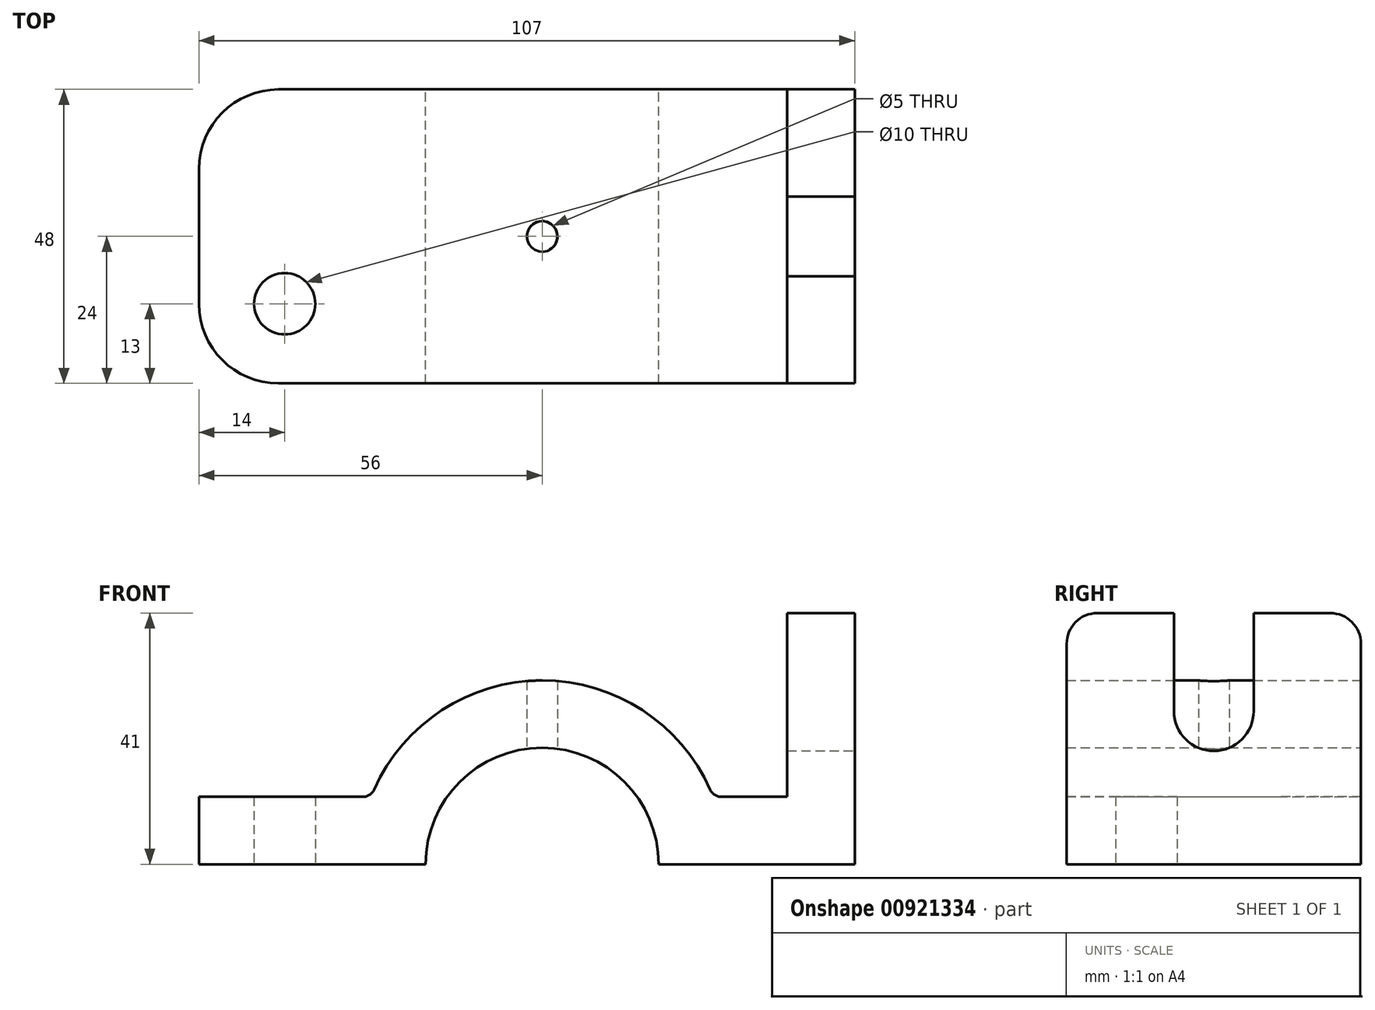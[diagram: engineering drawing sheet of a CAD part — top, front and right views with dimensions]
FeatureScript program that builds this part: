
annotation { "Feature Type Name" : "Feature", "Feature Type Description" : "" }
export const myFeature = defineFeature(function(context is Context, id is Id, definition is map)
    precondition{}
    {
        {
            var Q0;
            Q0=qCreatedBy(makeId("Front.planeOp"),FACE);
            var sketch = newSketch(context, id + "F0", { "sketchPlane" : qUnion([Q0])});
            skCircle(sketch, "E0", {"center": v(0, 0) * mm, "radius": 19 * mm});
            skCircle(sketch, "E1", {"center": v(0, 0) * mm, "radius": 30 * mm});
            skLineSegment(sketch, "E2.bottom", {"start": v(-56, 0) * mm, "end": v(51, 0) * mm});
            skLineSegment(sketch, "E2.top", {"start": v(-56, 11) * mm, "end": v(51, 11) * mm});
            skLineSegment(sketch, "E2.left", {"start": v(-56, 0) * mm, "end": v(-56, 11) * mm});
            skLineSegment(sketch, "E2.right", {"start": v(51, 0) * mm, "end": v(51, 11) * mm});
            skPoint(sketch, "E3", {"position": v(-2.5, 0) * mm});
            skLineSegment(sketch, "E4.bottom", {"start": v(51, 11) * mm, "end": v(40, 11) * mm});
            skLineSegment(sketch, "E4.top", {"start": v(51, 41) * mm, "end": v(40, 41) * mm});
            skLineSegment(sketch, "E4.left", {"start": v(51, 11) * mm, "end": v(51, 41) * mm});
            skLineSegment(sketch, "E4.right", {"start": v(40, 11) * mm, "end": v(40, 41) * mm});
            skSolve(sketch);
        }
        {
            var Q0;
            {var subQ5=sQuery(id+"F0.wireOp",EDGE,"E2.left");Q0=makeQuery(id+"F0.imprint","IMPRINT",FACE,{"disambiguationData":[TD([[makeQuery(id+"F0.imprint","IMPRINT",EDGE,{"derivedFrom":subQ5}),-1.0]])]});}
            var Q1;
            {var subQ0=sQuery(id+"F0.wireOp",EDGE,"E2.bottom");var subQ1=sQuery(id+"F0.wireOp",EDGE,"E0");var subQ2=makeQuery(id+"F0.imprint","INTERSECT",VERTEX,{"disambiguationData":[OD(0.0)],"derivedFrom":[subQ1,subQ0]});Q1=makeQuery(id+"F0.imprint","IMPRINT",FACE,{"disambiguationData":[TD([[makeQuery(id+"F0.imprint","IMPRINT",EDGE,{"disambiguationData":[TD([[subQ2,1.0]])],"derivedFrom":subQ1}),-1.0]])]});}
            var Q2;
            {var subQ0=sQuery(id+"F0.wireOp",EDGE,"E2.top");var subQ1=sQuery(id+"F0.wireOp",EDGE,"E0");var subQ2=makeQuery(id+"F0.imprint","INTERSECT",VERTEX,{"disambiguationData":[OD(0.0)],"derivedFrom":[subQ1,subQ0]});Q2=makeQuery(id+"F0.imprint","IMPRINT",FACE,{"disambiguationData":[TD([[makeQuery(id+"F0.imprint","IMPRINT",EDGE,{"disambiguationData":[TD([[subQ2,1.0]])],"derivedFrom":subQ1}),-1.0]])]});}
            var Q3;
            {var subQ0=sQuery(id+"F0.wireOp",EDGE,"E2.top");var subQ1=sQuery(id+"F0.wireOp",EDGE,"E0");var subQ2=makeQuery(id+"F0.imprint","INTERSECT",VERTEX,{"disambiguationData":[OD(1.0)],"derivedFrom":[subQ1,subQ0]});Q3=makeQuery(id+"F0.imprint","IMPRINT",FACE,{"disambiguationData":[TD([[makeQuery(id+"F0.imprint","IMPRINT",EDGE,{"disambiguationData":[TD([[subQ2,1.0]])],"derivedFrom":subQ1}),-1.0]])]});}
            var Q4;
            Q4=makeQuery(id+"F0.imprint","IMPRINT",FACE,{"disambiguationData":[TD([[makeQuery(id+"F0.imprint","IMPRINT",EDGE,{"derivedFrom":sQuery(id+"F0.wireOp",EDGE,"E4.top")}),1.0]])]});
            var Q5;
            {var subQ0=sQuery(id+"F0.wireOp",EDGE,"E2.right");Q5=makeQuery(id+"F0.imprint","IMPRINT",FACE,{"disambiguationData":[TD([[makeQuery(id+"F0.imprint","IMPRINT",EDGE,{"derivedFrom":subQ0}),1.0]])]});}
            extrude(context, id + "F1", {"entities" : qUnion([Q0, Q1, Q2, Q3, Q4, Q5]), "endBound" : BoundingType.SYMMETRIC, "depth" : 48 * mm, "offsetDistance" : 25 * mm});
        }
        {
            var Q0;
            Q0=makeQuery(id+"F1.opExtrude","SWEPT_FACE",FACE,{"disambiguationData":[OSD([sQuery(id+"F0.wireOp",EDGE,"E2.right"),sQuery(id+"F0.wireOp",EDGE,"E4.left")])]});
            var sketch = newSketch(context, id + "F2", { "sketchPlane" : qUnion([Q0])});
            skCircle(sketch, "E5", {"center": v(0, 25) * mm, "radius": 6.5 * mm});
            skLineSegment(sketch, "E6", {"start": v(0, 0) * mm, "end": v(0, 52.88) * mm, "construction": true});
            skLineSegment(sketch, "E7", {"start": v(-6.5, 25) * mm, "end": v(-6.5, 41) * mm});
            skLineSegment(sketch, "E8.MirrorCS", {"start": v(6.5, 25) * mm, "end": v(6.5, 41) * mm});
            skSolve(sketch);
        }
        {
            var Q0;
            {var subQ0=sQuery(id+"F2.wireOp",EDGE,"E7");Q0=makeQuery(id+"F2.imprint","IMPRINT",FACE,{"disambiguationData":[TD([[makeQuery(id+"F2.imprint","IMPRINT",EDGE,{"derivedFrom":subQ0}),-1.0]])]});}
            var Q1;
            {var subQ0=sQuery(id+"F2.wireOp",EDGE,"E5");var subQ1=makeQuery(id+"F2.imprint","INTERSECT",VERTEX,{"derivedFrom":[subQ0,sQuery(id+"F2.wireOp",EDGE,"E7")]});Q1=makeQuery(id+"F2.imprint","IMPRINT",FACE,{"disambiguationData":[TD([[makeQuery(id+"F2.imprint","IMPRINT",EDGE,{"disambiguationData":[TD([[subQ1,1.0]])],"derivedFrom":subQ0}),1.0]])]});}
            var Q2;
            Q2=makeQuery(id+"F1.opExtrude","SWEPT_FACE",FACE,{"disambiguationData":[OSD([sQuery(id+"F0.wireOp",EDGE,"E4.right")])]});
            extrude(context, id + "F3", {"entities" : qUnion([Q0, Q1]), "operationType" : NewBodyOperationType.REMOVE, "endBound" : BoundingType.UP_TO_SURFACE, "oppositeDirection" : true, "depth" : 25 * mm, "endBoundEntityFace" : qUnion([Q2]), "offsetDistance" : 25 * mm});
        }
        {
            var Q0;
            Q0=qCreatedBy(makeId("Top.planeOp"),FACE);
            var sketch = newSketch(context, id + "F4", { "sketchPlane" : qUnion([Q0])});
            skLineSegment(sketch, "E9", {"start": v(0, 0) * mm, "end": v(-40.77, 0) * mm, "construction": true});
            skCircle(sketch, "E10", {"center": v(-42, -11) * mm, "radius": 5 * mm});
            skCircle(sketch, "E11", {"center": v(0, 0) * mm, "radius": 2.5 * mm});
            skCircle(sketch, "E12.MirrorC", {"center": v(-42, 11) * mm, "radius": 5 * mm});
            skSolve(sketch);
        }
        {
            var Q0;
            Q0=makeQuery(id+"F4.imprint","IMPRINT",FACE,{"disambiguationData":[TD([[makeQuery(id+"F4.imprint","IMPRINT",EDGE,{"derivedFrom":sQuery(id+"F4.wireOp",EDGE,"E12.MirrorC")}),-1.0]])]});
            var Q1;
            Q1=makeQuery(id+"F4.imprint","IMPRINT",FACE,{"disambiguationData":[TD([[makeQuery(id+"F4.imprint","IMPRINT",EDGE,{"derivedFrom":sQuery(id+"F4.wireOp",EDGE,"E10")}),1.0]])]});
            var Q2;
            Q2=makeQuery(id+"F4.imprint","IMPRINT",FACE,{"disambiguationData":[TD([[makeQuery(id+"F4.imprint","IMPRINT",EDGE,{"derivedFrom":sQuery(id+"F4.wireOp",EDGE,"E11")}),1.0]])]});
            extrude(context, id + "F5", {"entities" : qUnion([Q0, Q1, Q2]), "operationType" : NewBodyOperationType.REMOVE, "endBound" : BoundingType.THROUGH_ALL, "depth" : 25 * mm, "offsetDistance" : 25 * mm});
        }
        {
            var Q0;
            Q0=makeQuery(id+"F1.opExtrude","CAP_EDGE",EDGE,{"disambiguationData":[OSD([sQuery(id+"F0.wireOp",EDGE,"E2.left")])],"isStart":false});
            var Q1;
            Q1=makeQuery(id+"F1.opExtrude","CAP_EDGE",EDGE,{"disambiguationData":[OSD([sQuery(id+"F0.wireOp",EDGE,"E2.left")])],"isStart":true});
            fillet(context, id + "F6", {"entities" : qUnion([Q0, Q1]), "radius" : 13 * mm, "tangentPropagation" : true, "allowEdgeOverflow" : false});
        }
        {
            var Q0;
            Q0=makeQuery(id+"F1.opExtrude","CAP_EDGE",EDGE,{"disambiguationData":[OSD([sQuery(id+"F0.wireOp",EDGE,"E4.top")])],"isStart":true});
            var Q1;
            Q1=makeQuery(id+"F1.opExtrude","CAP_EDGE",EDGE,{"disambiguationData":[OSD([sQuery(id+"F0.wireOp",EDGE,"E4.top")])],"isStart":false});
            fillet(context, id + "F7", {"entities" : qUnion([Q0, Q1]), "radius" : 5 * mm, "tangentPropagation" : true, "allowEdgeOverflow" : false});
        }
        {
            var Q0;
            {var subQ0=sQuery(id+"F0.wireOp",EDGE,"E2.top");var subQ1=sQuery(id+"F0.wireOp",EDGE,"E1");Q0=makeQuery(id+"F1.opExtrude","SWEPT_EDGE",EDGE,{"disambiguationData":[OSD([subQ1,subQ0]),TDD([makeQuery(id+"F0.imprint","INTERSECT",VERTEX,{"disambiguationData":[OD(1.0)],"derivedFrom":[subQ1,subQ0]})])]});}
            var Q1;
            {var subQ0=sQuery(id+"F0.wireOp",EDGE,"E2.top");var subQ1=sQuery(id+"F0.wireOp",EDGE,"E1");Q1=makeQuery(id+"F1.opExtrude","SWEPT_EDGE",EDGE,{"disambiguationData":[OSD([subQ1,subQ0]),TDD([makeQuery(id+"F0.imprint","INTERSECT",VERTEX,{"disambiguationData":[OD(0.0)],"derivedFrom":[subQ1,subQ0]})])]});}
            fillet(context, id + "F8", {"entities" : qUnion([Q0, Q1]), "radius" : 2 * mm, "tangentPropagation" : true, "allowEdgeOverflow" : false});
        }
    });
